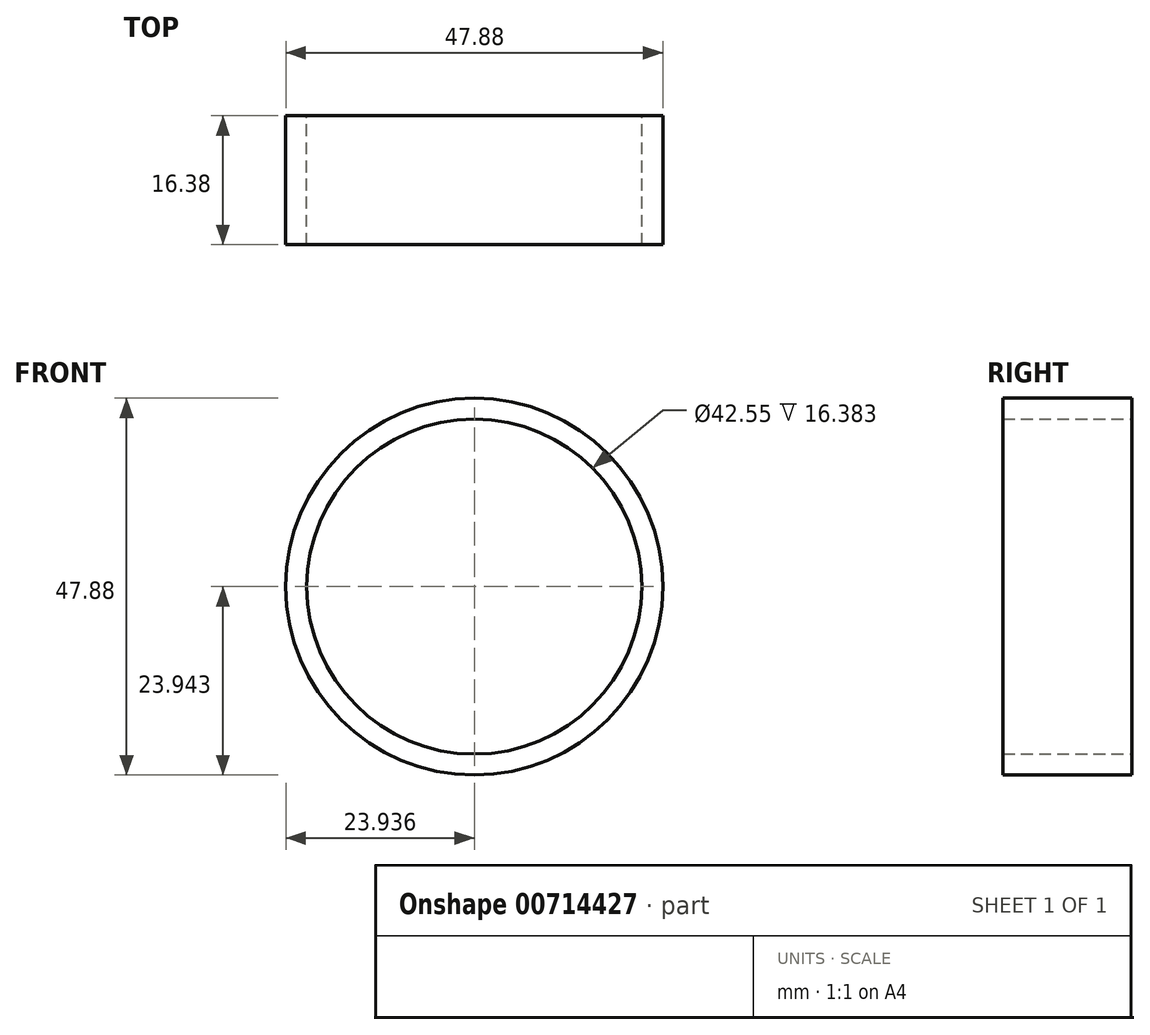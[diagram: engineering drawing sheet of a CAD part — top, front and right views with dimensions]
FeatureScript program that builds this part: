
annotation { "Feature Type Name" : "Feature", "Feature Type Description" : "" }
export const myFeature = defineFeature(function(context is Context, id is Id, definition is map)
    precondition{}
    {
        {
            var Q0;
            Q0=qCreatedBy(makeId("Front.planeOp"),FACE);
            var sketch = newSketch(context, id + "F0", { "sketchPlane" : qUnion([Q0])});
            skCircle(sketch, "E0", {"center": v(-140.86, 75.2) * mm, "radius": 23.94 * mm});
            skCircle(sketch, "E1", {"center": v(-140.86, 75.2) * mm, "radius": 21.27 * mm});
            skSolve(sketch);
        }
        {
            var Q0;
            Q0 = qSketchRegion(id + "F0", true);
            extrude(context, id + "F1", {"entities" : qUnion([Q0]), "depth" : 16.38 * mm, "offsetDistance" : 25.4 * mm});
        }
    });
